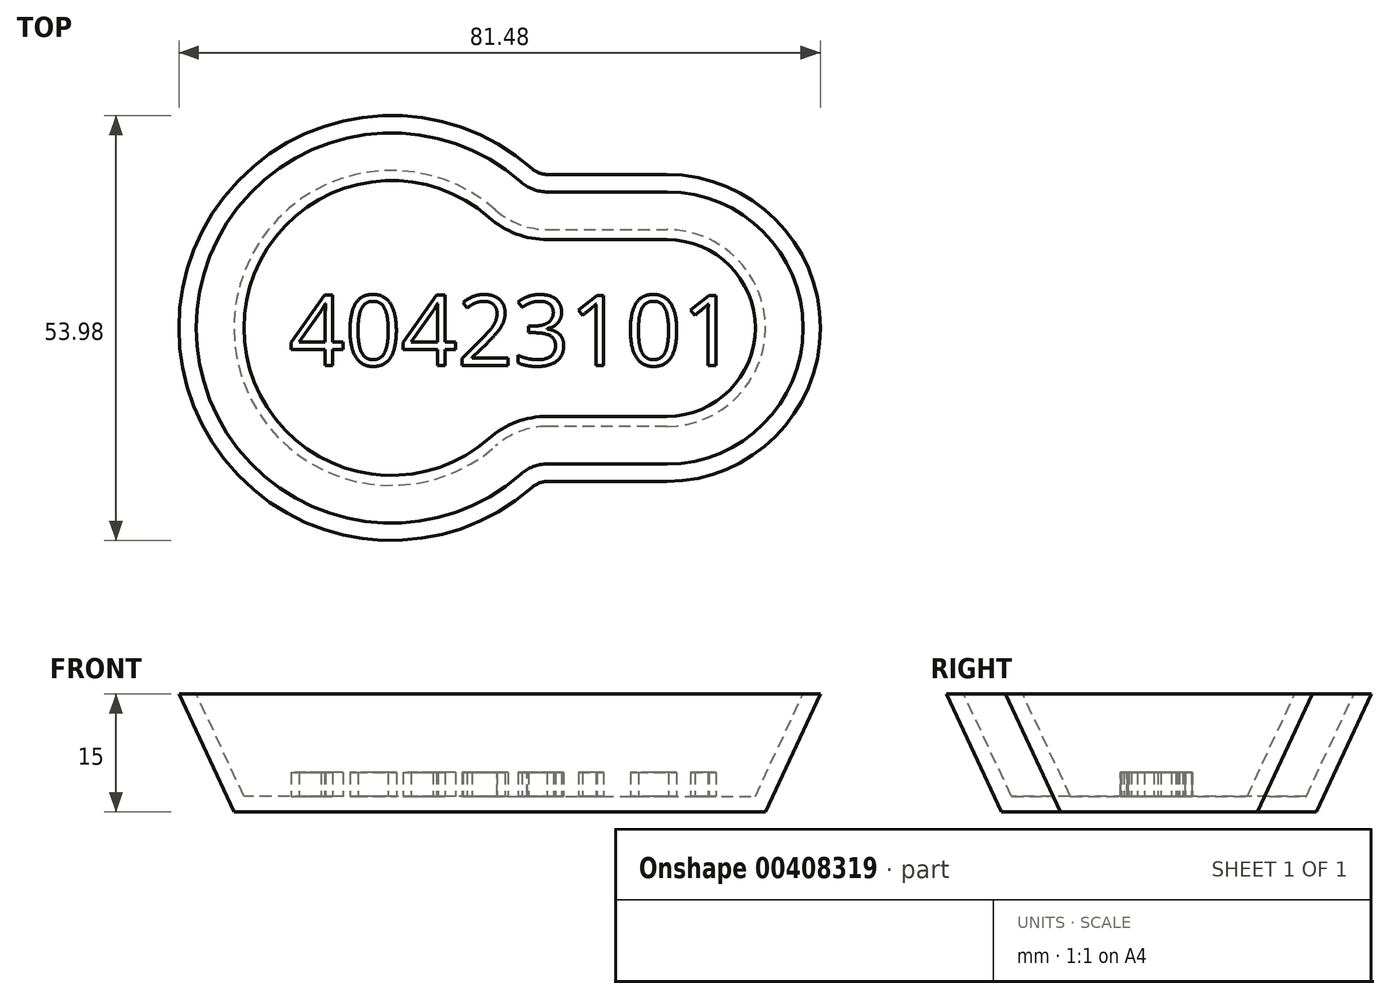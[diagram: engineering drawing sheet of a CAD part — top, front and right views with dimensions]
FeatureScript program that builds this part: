
annotation { "Feature Type Name" : "Feature", "Feature Type Description" : "" }
export const myFeature = defineFeature(function(context is Context, id is Id, definition is map)
    precondition{}
    {
        {
            var Q0;
            Q0=qCreatedBy(makeId("Top.planeOp"),FACE);
            var sketch = newSketch(context, id + "F0", { "sketchPlane" : qUnion([Q0])});
            skArc(sketch, "E0", {"start": v(-6.77, 15) * mm, "mid": v(-40, 0) * mm, "end": v(-6.77, -15) * mm});
            skArc(sketch, "E1", {"start": v(15, -12.5) * mm, "mid": v(27.5, 0) * mm, "end": v(15, 12.5) * mm});
            skLineSegment(sketch, "E2", {"start": v(15, 12.5) * mm, "end": v(-0.16, 12.5) * mm});
            skLineSegment(sketch, "E3", {"start": v(15, -12.5) * mm, "end": v(-0.16, -12.5) * mm});
            skPoint(sketch, "E4.visualSharp", {"position": v(-4.39, 12.5) * mm});
            skArc(sketch, "E4.filletArc", {"start": v(-6.77, 15) * mm, "mid": v(-3.7, 13.15) * mm, "end": v(-0.16, 12.5) * mm});
            skPoint(sketch, "E5.visualSharp", {"position": v(-4.39, -12.5) * mm});
            skArc(sketch, "E5.filletArc", {"start": v(-0.16, -12.5) * mm, "mid": v(-3.7, -13.15) * mm, "end": v(-6.77, -15) * mm});
            skSolve(sketch);
        }
        {
            var Q0;
            Q0 = qSketchRegion(id + "F0", true);
            extrude(context, id + "F1", {"entities" : qUnion([Q0]), "depth" : 15 * mm, "hasDraft" : true, "draftAngle" : 25 * degree});
        }
        {
            var Q0;
            Q0=makeQuery(id+"F1.opExtrude","CAP_FACE",FACE,{"disambiguationData":[OSD([sQuery(id+"F0.wireOp",EDGE,"E0"),sQuery(id+"F0.wireOp",EDGE,"E1"),sQuery(id+"F0.wireOp",EDGE,"E2"),sQuery(id+"F0.wireOp",EDGE,"E3"),sQuery(id+"F0.wireOp",EDGE,"E4.filletArc"),sQuery(id+"F0.wireOp",EDGE,"E5.filletArc")])],"isStart":false});
            shell(context, id + "F2", {"entities" : qUnion([Q0]), "thickness" : 2 * mm});
        }
        {
            var Q0;
            Q0=makeQuery(id+"F2.opShell","OFFSET_FACE",FACE,{"disambiguationData":[OSD([sQuery(id+"F0.wireOp",EDGE,"E0"),sQuery(id+"F0.wireOp",EDGE,"E1"),sQuery(id+"F0.wireOp",EDGE,"E2"),sQuery(id+"F0.wireOp",EDGE,"E3"),sQuery(id+"F0.wireOp",EDGE,"E4.filletArc"),sQuery(id+"F0.wireOp",EDGE,"E5.filletArc")])]});
            var sketch = newSketch(context, id + "F3", { "sketchPlane" : qUnion([Q0])});
            skText(sketch, "E6", { "text": "40423101", "fontName": "OpenSans-Regular.ttf"});
            const initialGuessF3  = {"E6": [-0.033, -0.00477, 1, 0, 0.00897]};
            skSetInitialGuess(sketch, initialGuessF3);
            skSolve(sketch);
        }
        {
            var Q0;
            Q0 = qSketchRegion(id + "F3", true);
            extrude(context, id + "F4", {"entities" : qUnion([Q0]), "operationType" : NewBodyOperationType.ADD, "depth" : 3 * mm});
        }
    });
